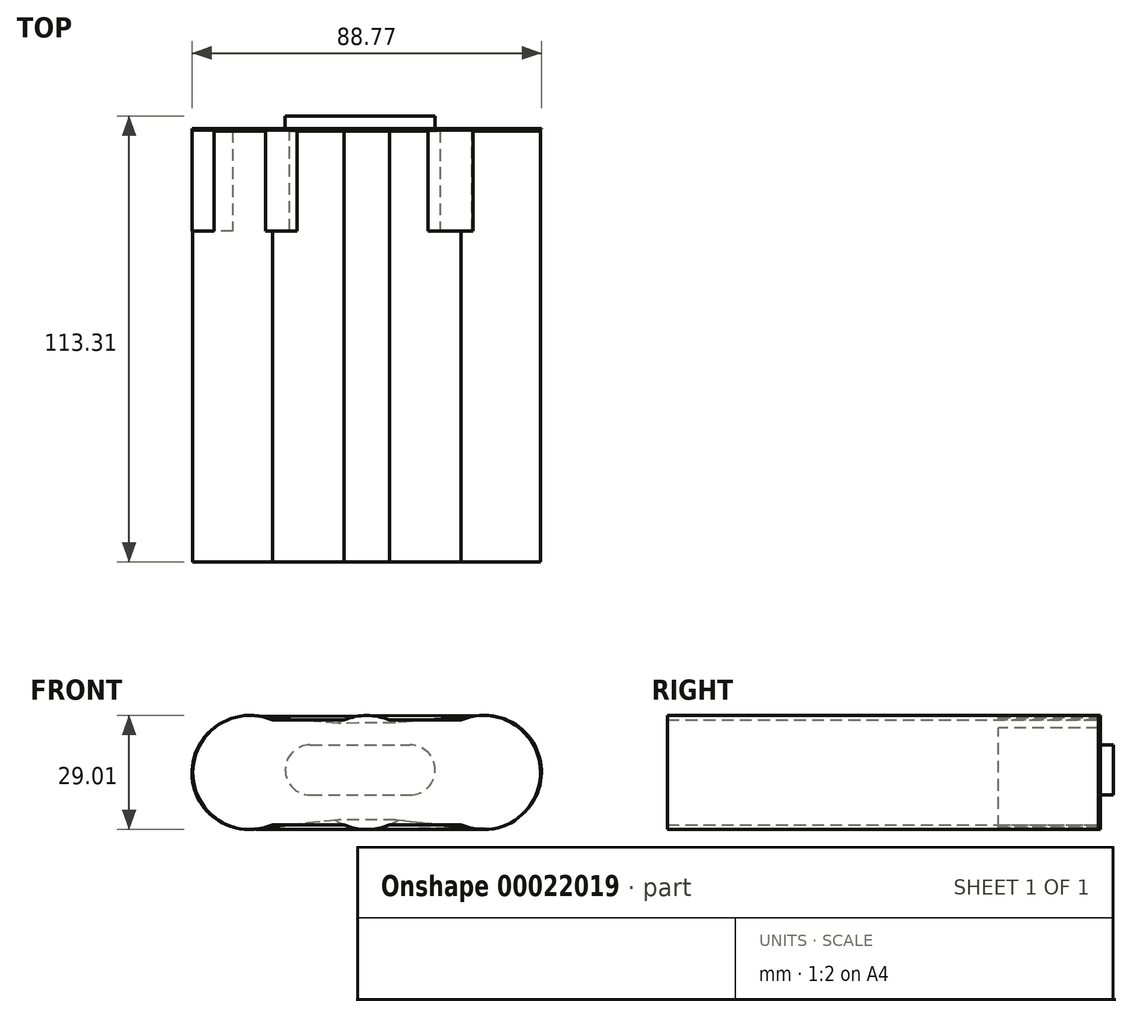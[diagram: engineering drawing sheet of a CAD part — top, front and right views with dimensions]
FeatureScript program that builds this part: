
annotation { "Feature Type Name" : "Feature", "Feature Type Description" : "" }
export const myFeature = defineFeature(function(context is Context, id is Id, definition is map)
    precondition{}
    {
        {
            var Q0;
            Q0=qCreatedBy(makeId("Front.planeOp"),FACE);
            var sketch = newSketch(context, id + "F0", { "sketchPlane" : qUnion([Q0])});
            skCircle(sketch, "E0", {"center": v(-38.75, 5.62) * mm, "radius": 14.5 * mm});
            skCircle(sketch, "E1", {"center": v(-9.06, 5.62) * mm, "radius": 14.5 * mm});
            skCircle(sketch, "E2", {"center": v(20.63, 5.62) * mm, "radius": 14.5 * mm});
            skLineSegment(sketch, "E3", {"start": v(-38.75, 5.62) * mm, "end": v(-9.06, 5.62) * mm});
            skLineSegment(sketch, "E4", {"start": v(-9.06, 5.62) * mm, "end": v(20.63, 5.62) * mm});
            skSolve(sketch);
        }
        {
            var Q0;
            Q0 = qSketchRegion(id + "F0", true);
            extrude(context, id + "F1", {"entities" : qUnion([Q0]), "depth" : 109.5 * mm});
        }
        {
            var Q0;
            Q0=makeQuery(id+"F1.opExtrude","CAP_FACE",FACE,{"disambiguationData":[OSD([sQuery(id+"F0.wireOp",EDGE,"E0")])],"isStart":false});
            var sketch = newSketch(context, id + "F2", { "sketchPlane" : qUnion([Q0])});
            skLineSegment(sketch, "E5", {"start": v(-33, 18.94) * mm, "end": v(17.07, 18.94) * mm});
            skLineSegment(sketch, "E6", {"start": v(-33, 18.94) * mm, "end": v(-33, -7.7) * mm});
            skLineSegment(sketch, "E7", {"start": v(-33, -7.7) * mm, "end": v(17.07, -7.7) * mm});
            skLineSegment(sketch, "E8", {"start": v(17.07, -7.7) * mm, "end": v(17.07, 18.94) * mm});
            skSolve(sketch);
        }
        {
            var Q0;
            Q0 = qSketchRegion(id + "F2", true);
            extrude(context, id + "F3", {"entities" : qUnion([Q0]), "operationType" : NewBodyOperationType.ADD, "oppositeDirection" : true, "depth" : 109.22 * mm});
        }
        {
            var Q0;
            {var subQ0=sQuery(id+"F2.wireOp",EDGE,"E5");var subQ1=sQuery(id+"F2.wireOp",EDGE,"E7");Q0=makeQuery(id+"F3.boolean.opBoolean","SPLIT",FACE,{"disambiguationData":[TD([makeQuery(id+"F1.opExtrude","SWEPT_FACE",FACE,{"disambiguationData":[OSD([sQuery(id+"F0.wireOp",EDGE,"E2")])]})])],"derivedFrom":makeQuery(id+"F3.opExtrude","CAP_FACE",FACE,{"disambiguationData":[OSD([subQ0,sQuery(id+"F2.wireOp",EDGE,"E6"),subQ1,sQuery(id+"F2.wireOp",EDGE,"E8")])],"isStart":false})});}
            var Q1;
            {var subQ0=sQuery(id+"F2.wireOp",EDGE,"E5");var subQ1=sQuery(id+"F2.wireOp",EDGE,"E7");Q1=makeQuery(id+"F3.boolean.opBoolean","SPLIT",FACE,{"disambiguationData":[TD([makeQuery(id+"F1.opExtrude","SWEPT_FACE",FACE,{"disambiguationData":[OSD([sQuery(id+"F0.wireOp",EDGE,"E0")])]})])],"derivedFrom":makeQuery(id+"F3.opExtrude","CAP_FACE",FACE,{"disambiguationData":[OSD([subQ0,sQuery(id+"F2.wireOp",EDGE,"E6"),subQ1,sQuery(id+"F2.wireOp",EDGE,"E8")])],"isStart":false})});}
            extrude(context, id + "F4", {"entities" : qUnion([Q0, Q1]), "operationType" : NewBodyOperationType.ADD, "depth" : 0.25 * mm});
        }
        {
            var Q0;
            Q0=makeQuery(id+"F1.opExtrude","CAP_FACE",FACE,{"disambiguationData":[OSD([sQuery(id+"F0.wireOp",EDGE,"E2")])],"isStart":true});
            var sketch = newSketch(context, id + "F5", { "sketchPlane" : qUnion([Q0])});
            skArc(sketch, "E9", {"start": v(-20.92, 20.12) * mm, "mid": v(-35.04, 5.37) * mm, "end": v(-20.4, -8.87) * mm});
            skArc(sketch, "E10", {"start": v(39.48, -8.79) * mm, "mid": v(53.42, 5.73) * mm, "end": v(39.14, 19.92) * mm});
            skLineSegment(sketch, "E11", {"start": v(-20.92, 20.12) * mm, "end": v(1.8, 18.26) * mm});
            skLineSegment(sketch, "E12", {"start": v(16.08, 18.1) * mm, "end": v(39.14, 19.92) * mm});
            skLineSegment(sketch, "E13", {"start": v(-20.4, -8.87) * mm, "end": v(1.8, -6.46) * mm});
            skLineSegment(sketch, "E14", {"start": v(1.8, -6.46) * mm, "end": v(16.4, -6.46) * mm});
            skLineSegment(sketch, "E15", {"start": v(16.4, -6.46) * mm, "end": v(39.48, -8.79) * mm});
            skLineSegment(sketch, "E16", {"start": v(1.8, 18.26) * mm, "end": v(16.08, 18.1) * mm});
            skSolve(sketch);
        }
        {
            var Q0;
            Q0 = qSketchRegion(id + "F5", true);
            extrude(context, id + "F6", {"entities" : qUnion([Q0]), "operationType" : NewBodyOperationType.ADD, "depth" : 0.25 * mm, "hasSecondDirection" : true, "secondDirectionOppositeDirection" : true, "secondDirectionDepth" : 25.4 * mm});
        }
        {
            var Q0;
            Q0=qCreatedBy(makeId("Front.planeOp"),FACE);
            cPlane(context, id + "F7", {"entities" : qUnion([Q0]), "cplaneType" : CPlaneType.OFFSET, "offset" : 3.8 * mm, "oppositeDirection" : true, "width" : 152.4 * mm, "height" : 152.4 * mm});
        }
        {
            var Q0;
            Q0=qCreatedBy(id+"F7.planeOp",FACE);
            var sketch = newSketch(context, id + "F8", { "sketchPlane" : qUnion([Q0])});
            skLineSegment(sketch, "E17", {"start": v(1.98, 12.61) * mm, "end": v(-23.42, 12.61) * mm});
            skLineSegment(sketch, "E18", {"start": v(1.98, -0.09) * mm, "end": v(-23.42, -0.09) * mm});
            skArc(sketch, "E19", {"start": v(1.98, -0.09) * mm, "mid": v(8.33, 6.26) * mm, "end": v(1.98, 12.61) * mm});
            skArc(sketch, "E20", {"start": v(-23.42, 12.61) * mm, "mid": v(-29.77, 6.26) * mm, "end": v(-23.42, -0.09) * mm});
            skSolve(sketch);
        }
        {
            var Q0;
            Q0 = qSketchRegion(id + "F8", true);
            extrude(context, id + "F9", {"entities" : qUnion([Q0]), "operationType" : NewBodyOperationType.ADD, "depth" : 25.4 * mm});
        }
        {
            var Q0;
            Q0=makeQuery(id+"F6.opExtrude","CAP_FACE",FACE,{"disambiguationData":[OSD([sQuery(id+"F5.wireOp",EDGE,"E9"),sQuery(id+"F5.wireOp",EDGE,"E10"),sQuery(id+"F5.wireOp",EDGE,"E11"),sQuery(id+"F5.wireOp",EDGE,"E12"),sQuery(id+"F5.wireOp",EDGE,"E13"),sQuery(id+"F5.wireOp",EDGE,"E14"),sQuery(id+"F5.wireOp",EDGE,"E15"),sQuery(id+"F5.wireOp",EDGE,"E16")])],"isStart":false});
            var sketch = newSketch(context, id + "F10", { "sketchPlane" : qUnion([Q0])});
            skLineSegment(sketch, "E21", {"start": v(-20.92, 20.12) * mm, "end": v(39.14, 19.92) * mm});
            skLineSegment(sketch, "E22", {"start": v(-20.4, -8.87) * mm, "end": v(39.48, -8.79) * mm});
            skArc(sketch, "E23", {"start": v(39.48, -8.79) * mm, "mid": v(53.45, 5.73) * mm, "end": v(39.14, 19.92) * mm});
            skArc(sketch, "E24", {"start": v(-20.92, 20.12) * mm, "mid": v(-34.92, 5.37) * mm, "end": v(-20.4, -8.87) * mm});
            skSolve(sketch);
        }
        {
            var Q0;
            Q0 = qSketchRegion(id + "F10", true);
            extrude(context, id + "F11", {"entities" : qUnion([Q0]), "operationType" : NewBodyOperationType.ADD, "depth" : 0.25 * mm});
        }
        {
            var Q0;
            Q0=makeQuery(id+"F11.opExtrude","CAP_FACE",FACE,{"disambiguationData":[OSD([sQuery(id+"F10.wireOp",EDGE,"E21"),sQuery(id+"F10.wireOp",EDGE,"E22"),sQuery(id+"F10.wireOp",EDGE,"E23"),sQuery(id+"F10.wireOp",EDGE,"E24")])],"isStart":false});
            var sketch = newSketch(context, id + "F12", { "sketchPlane" : qUnion([Q0])});
            skLineSegment(sketch, "E25", {"start": v(39.14, 19.92) * mm, "end": v(39.19, -8.79) * mm});
            skLineSegment(sketch, "E26", {"start": v(-20.92, 20.12) * mm, "end": v(-20.92, -8.58) * mm});
            skArc(sketch, "E27", {"start": v(-20.92, 20.12) * mm, "mid": v(-35.32, 5.77) * mm, "end": v(-20.92, -8.58) * mm});
            skArc(sketch, "E28", {"start": v(39.48, -8.79) * mm, "mid": v(53.45, 5.73) * mm, "end": v(39.14, 19.92) * mm});
            skLineSegment(sketch, "E29", {"start": v(-20.92, -8.58) * mm, "end": v(39.48, -8.79) * mm});
            skLineSegment(sketch, "E30", {"start": v(-20.92, 20.12) * mm, "end": v(39.14, 19.92) * mm});
            skSolve(sketch);
        }
        {
            var Q0;
            Q0 = qSketchRegion(id + "F12", true);
            extrude(context, id + "F13", {"entities" : qUnion([Q0]), "operationType" : NewBodyOperationType.ADD, "depth" : 0.03 * mm});
        }
    });
